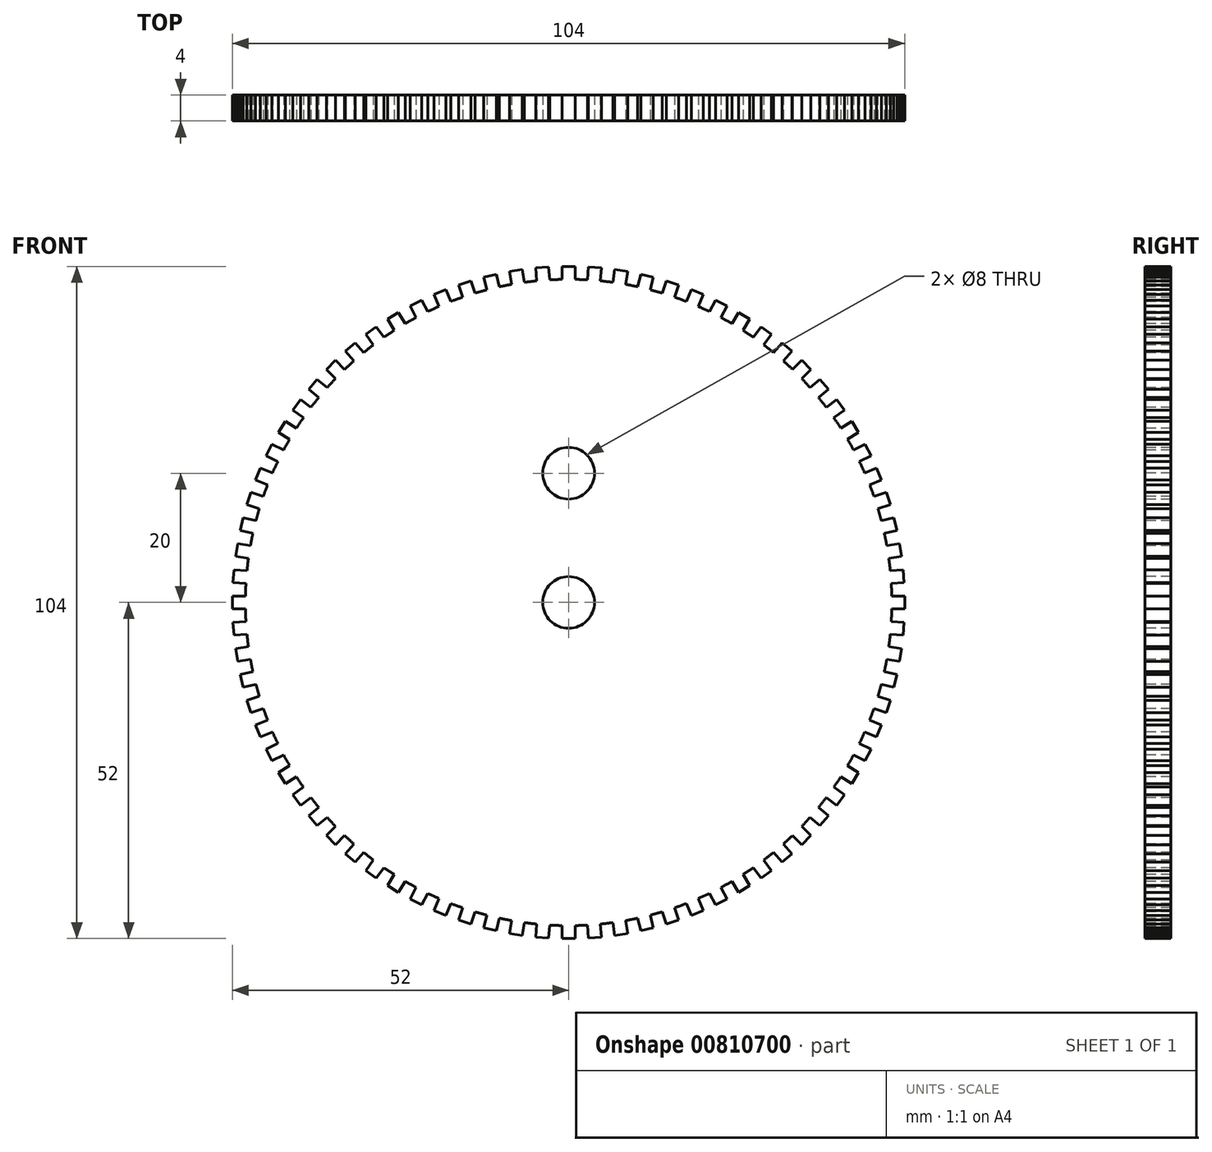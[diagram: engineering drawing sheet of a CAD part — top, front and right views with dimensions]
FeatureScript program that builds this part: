
annotation { "Feature Type Name" : "Feature", "Feature Type Description" : "" }
export const myFeature = defineFeature(function(context is Context, id is Id, definition is map)
    precondition{}
    {
        {
            var Q0;
            Q0=qCreatedBy(makeId("Front.planeOp"),FACE);
            var sketch = newSketch(context, id + "F0", { "sketchPlane" : qUnion([Q0])});
            skCircle(sketch, "E0", {"center": v(0, 0) * mm, "radius": 50 * mm});
            skSolve(sketch);
        }
        {
            var Q0;
            Q0=makeQuery(id+"F0.imprint","IMPRINT",FACE,{"disambiguationData":[TD([[makeQuery(id+"F0.imprint","IMPRINT",EDGE,{"derivedFrom":sQuery(id+"F0.wireOp",EDGE,"E0")}),1.0]])]});
            extrude(context, id + "F1", {"entities" : qUnion([Q0]), "depth" : 4 * mm, "offsetDistance" : 25 * mm});
        }
        {
            var Q0;
            Q0=makeQuery(id+"F1.opExtrude","CAP_FACE",FACE,{"disambiguationData":[OSD([sQuery(id+"F0.wireOp",EDGE,"E0")])],"isStart":false});
            var sketch = newSketch(context, id + "F2", { "sketchPlane" : qUnion([Q0])});
            skLineSegment(sketch, "E1", {"start": v(-1.96, 20) * mm, "end": v(3.56, 20) * mm});
            skCircle(sketch, "E2", {"center": v(0, 20) * mm, "radius": 4 * mm});
            skSolve(sketch);
        }
        {
            var Q0;
            Q0=makeQuery(id+"F2.imprint","IMPRINT",FACE,{"disambiguationData":[TD([[makeQuery(id+"F2.imprint","IMPRINT",EDGE,{"derivedFrom":sQuery(id+"F2.wireOp",EDGE,"E2")}),1.0]])]});
            extrude(context, id + "F3", {"entities" : qUnion([Q0]), "operationType" : NewBodyOperationType.REMOVE, "oppositeDirection" : true, "depth" : 25 * mm, "offsetDistance" : 25 * mm});
        }
        {
            var Q0;
            Q0=makeQuery(id+"F1.opExtrude","CAP_FACE",FACE,{"disambiguationData":[OSD([sQuery(id+"F0.wireOp",EDGE,"E0")])],"isStart":false});
            var sketch = newSketch(context, id + "F4", { "sketchPlane" : qUnion([Q0])});
            skLineSegment(sketch, "E3", {"start": v(-52, 1) * mm, "end": v(-52, -1) * mm});
            skLineSegment(sketch, "E4", {"start": v(-52, -1) * mm, "end": v(-49.99, -1) * mm});
            skLineSegment(sketch, "E5", {"start": v(-52, 1) * mm, "end": v(-49.99, 1) * mm});
            skArc(sketch, "E6", {"start": v(-49.99, 1) * mm, "mid": v(-50, 0) * mm, "end": v(-49.99, -1) * mm});
            skSolve(sketch);
        }
        {
            var Q0;
            Q0 = qSketchRegion(id + "F4", true);
            extrude(context, id + "F5", {"entities" : qUnion([Q0]), "oppositeDirection" : true, "depth" : 4 * mm, "offsetDistance" : 25 * mm});
        }
        {
            var Q0;
            Q0=qCreatedBy(makeId("Right.planeOp"),FACE);
            var sketch = newSketch(context, id + "F6", { "sketchPlane" : qUnion([Q0])});
            skLineSegment(sketch, "E7", {"start": v(-13.13, 0) * mm, "end": v(9.1, 0) * mm, "construction": true});
            skSolve(sketch);
        }
        {
            var Q0;
            Q0=makeQuery(id+"F5.opExtrude","SWEPT_BODY",BODY,{"disambiguationData":[OSD([sQuery(id+"F4.wireOp",EDGE,"E3"),sQuery(id+"F4.wireOp",EDGE,"E4"),sQuery(id+"F4.wireOp",EDGE,"E5"),sQuery(id+"F4.wireOp",EDGE,"E6")])]});
            var Q1;
            Q1=sQuery(id+"F6.wireOp",EDGE,"E7");
            circularPattern(context, id + "F7", {"operationType" : NewBodyOperationType.ADD, "entities" : qUnion([Q0]), "axis" : qUnion([Q1]), "angle" : 360 * degree, "instanceCount" : 80, "equalSpace" : true});
        }
        {
            var Q0;
            {var subQ0=makeQuery(id+"F5.opExtrude","CAP_FACE",FACE,{"disambiguationData":[OSD([sQuery(id+"F4.wireOp",EDGE,"E3"),sQuery(id+"F4.wireOp",EDGE,"E4"),sQuery(id+"F4.wireOp",EDGE,"E5"),sQuery(id+"F4.wireOp",EDGE,"E6")])],"isStart":true});Q0=makeQuery(id+"F7.boolean.opBoolean","MERGE",FACE,{"derivedFrom":[makeQuery(id+"F1.opExtrude","CAP_FACE",FACE,{"disambiguationData":[OSD([sQuery(id+"F0.wireOp",EDGE,"E0")])],"isStart":false}),subQ0,makeQuery(id+"F7.opPattern","COPY",FACE,{"derivedFrom":subQ0,"instanceName":"1"}),makeQuery(id+"F7.opPattern","COPY",FACE,{"derivedFrom":subQ0,"instanceName":"2"}),makeQuery(id+"F7.opPattern","COPY",FACE,{"derivedFrom":subQ0,"instanceName":"3"}),makeQuery(id+"F7.opPattern","COPY",FACE,{"derivedFrom":subQ0,"instanceName":"4"}),makeQuery(id+"F7.opPattern","COPY",FACE,{"derivedFrom":subQ0,"instanceName":"5"}),makeQuery(id+"F7.opPattern","COPY",FACE,{"derivedFrom":subQ0,"instanceName":"6"}),makeQuery(id+"F7.opPattern","COPY",FACE,{"derivedFrom":subQ0,"instanceName":"7"}),makeQuery(id+"F7.opPattern","COPY",FACE,{"derivedFrom":subQ0,"instanceName":"8"}),makeQuery(id+"F7.opPattern","COPY",FACE,{"derivedFrom":subQ0,"instanceName":"9"}),makeQuery(id+"F7.opPattern","COPY",FACE,{"derivedFrom":subQ0,"instanceName":"10"}),makeQuery(id+"F7.opPattern","COPY",FACE,{"derivedFrom":subQ0,"instanceName":"11"}),makeQuery(id+"F7.opPattern","COPY",FACE,{"derivedFrom":subQ0,"instanceName":"12"}),makeQuery(id+"F7.opPattern","COPY",FACE,{"derivedFrom":subQ0,"instanceName":"13"}),makeQuery(id+"F7.opPattern","COPY",FACE,{"derivedFrom":subQ0,"instanceName":"14"}),makeQuery(id+"F7.opPattern","COPY",FACE,{"derivedFrom":subQ0,"instanceName":"15"}),makeQuery(id+"F7.opPattern","COPY",FACE,{"derivedFrom":subQ0,"instanceName":"16"}),makeQuery(id+"F7.opPattern","COPY",FACE,{"derivedFrom":subQ0,"instanceName":"17"}),makeQuery(id+"F7.opPattern","COPY",FACE,{"derivedFrom":subQ0,"instanceName":"18"}),makeQuery(id+"F7.opPattern","COPY",FACE,{"derivedFrom":subQ0,"instanceName":"19"}),makeQuery(id+"F7.opPattern","COPY",FACE,{"derivedFrom":subQ0,"instanceName":"20"}),makeQuery(id+"F7.opPattern","COPY",FACE,{"derivedFrom":subQ0,"instanceName":"21"}),makeQuery(id+"F7.opPattern","COPY",FACE,{"derivedFrom":subQ0,"instanceName":"22"}),makeQuery(id+"F7.opPattern","COPY",FACE,{"derivedFrom":subQ0,"instanceName":"23"}),makeQuery(id+"F7.opPattern","COPY",FACE,{"derivedFrom":subQ0,"instanceName":"24"}),makeQuery(id+"F7.opPattern","COPY",FACE,{"derivedFrom":subQ0,"instanceName":"25"}),makeQuery(id+"F7.opPattern","COPY",FACE,{"derivedFrom":subQ0,"instanceName":"26"}),makeQuery(id+"F7.opPattern","COPY",FACE,{"derivedFrom":subQ0,"instanceName":"27"}),makeQuery(id+"F7.opPattern","COPY",FACE,{"derivedFrom":subQ0,"instanceName":"28"}),makeQuery(id+"F7.opPattern","COPY",FACE,{"derivedFrom":subQ0,"instanceName":"29"}),makeQuery(id+"F7.opPattern","COPY",FACE,{"derivedFrom":subQ0,"instanceName":"30"}),makeQuery(id+"F7.opPattern","COPY",FACE,{"derivedFrom":subQ0,"instanceName":"31"}),makeQuery(id+"F7.opPattern","COPY",FACE,{"derivedFrom":subQ0,"instanceName":"32"}),makeQuery(id+"F7.opPattern","COPY",FACE,{"derivedFrom":subQ0,"instanceName":"33"}),makeQuery(id+"F7.opPattern","COPY",FACE,{"derivedFrom":subQ0,"instanceName":"34"}),makeQuery(id+"F7.opPattern","COPY",FACE,{"derivedFrom":subQ0,"instanceName":"35"}),makeQuery(id+"F7.opPattern","COPY",FACE,{"derivedFrom":subQ0,"instanceName":"36"}),makeQuery(id+"F7.opPattern","COPY",FACE,{"derivedFrom":subQ0,"instanceName":"37"}),makeQuery(id+"F7.opPattern","COPY",FACE,{"derivedFrom":subQ0,"instanceName":"38"}),makeQuery(id+"F7.opPattern","COPY",FACE,{"derivedFrom":subQ0,"instanceName":"39"}),makeQuery(id+"F7.opPattern","COPY",FACE,{"derivedFrom":subQ0,"instanceName":"40"}),makeQuery(id+"F7.opPattern","COPY",FACE,{"derivedFrom":subQ0,"instanceName":"41"}),makeQuery(id+"F7.opPattern","COPY",FACE,{"derivedFrom":subQ0,"instanceName":"42"}),makeQuery(id+"F7.opPattern","COPY",FACE,{"derivedFrom":subQ0,"instanceName":"43"}),makeQuery(id+"F7.opPattern","COPY",FACE,{"derivedFrom":subQ0,"instanceName":"44"}),makeQuery(id+"F7.opPattern","COPY",FACE,{"derivedFrom":subQ0,"instanceName":"45"}),makeQuery(id+"F7.opPattern","COPY",FACE,{"derivedFrom":subQ0,"instanceName":"46"}),makeQuery(id+"F7.opPattern","COPY",FACE,{"derivedFrom":subQ0,"instanceName":"47"}),makeQuery(id+"F7.opPattern","COPY",FACE,{"derivedFrom":subQ0,"instanceName":"48"}),makeQuery(id+"F7.opPattern","COPY",FACE,{"derivedFrom":subQ0,"instanceName":"49"}),makeQuery(id+"F7.opPattern","COPY",FACE,{"derivedFrom":subQ0,"instanceName":"50"}),makeQuery(id+"F7.opPattern","COPY",FACE,{"derivedFrom":subQ0,"instanceName":"51"}),makeQuery(id+"F7.opPattern","COPY",FACE,{"derivedFrom":subQ0,"instanceName":"52"}),makeQuery(id+"F7.opPattern","COPY",FACE,{"derivedFrom":subQ0,"instanceName":"53"}),makeQuery(id+"F7.opPattern","COPY",FACE,{"derivedFrom":subQ0,"instanceName":"54"}),makeQuery(id+"F7.opPattern","COPY",FACE,{"derivedFrom":subQ0,"instanceName":"55"}),makeQuery(id+"F7.opPattern","COPY",FACE,{"derivedFrom":subQ0,"instanceName":"56"}),makeQuery(id+"F7.opPattern","COPY",FACE,{"derivedFrom":subQ0,"instanceName":"57"}),makeQuery(id+"F7.opPattern","COPY",FACE,{"derivedFrom":subQ0,"instanceName":"58"}),makeQuery(id+"F7.opPattern","COPY",FACE,{"derivedFrom":subQ0,"instanceName":"59"})]});}
            var sketch = newSketch(context, id + "F8", { "sketchPlane" : qUnion([Q0])});
            skCircle(sketch, "E8", {"center": v(0, 0) * mm, "radius": 4 * mm});
            skSolve(sketch);
        }
        {
            var Q0;
            Q0=makeQuery(id+"F8.imprint","IMPRINT",FACE,{"disambiguationData":[TD([[makeQuery(id+"F8.imprint","IMPRINT",EDGE,{"derivedFrom":sQuery(id+"F8.wireOp",EDGE,"E8")}),1.0]])]});
            extrude(context, id + "F9", {"entities" : qUnion([Q0]), "operationType" : NewBodyOperationType.REMOVE, "oppositeDirection" : true, "depth" : 25 * mm, "offsetDistance" : 25 * mm});
        }
    });
